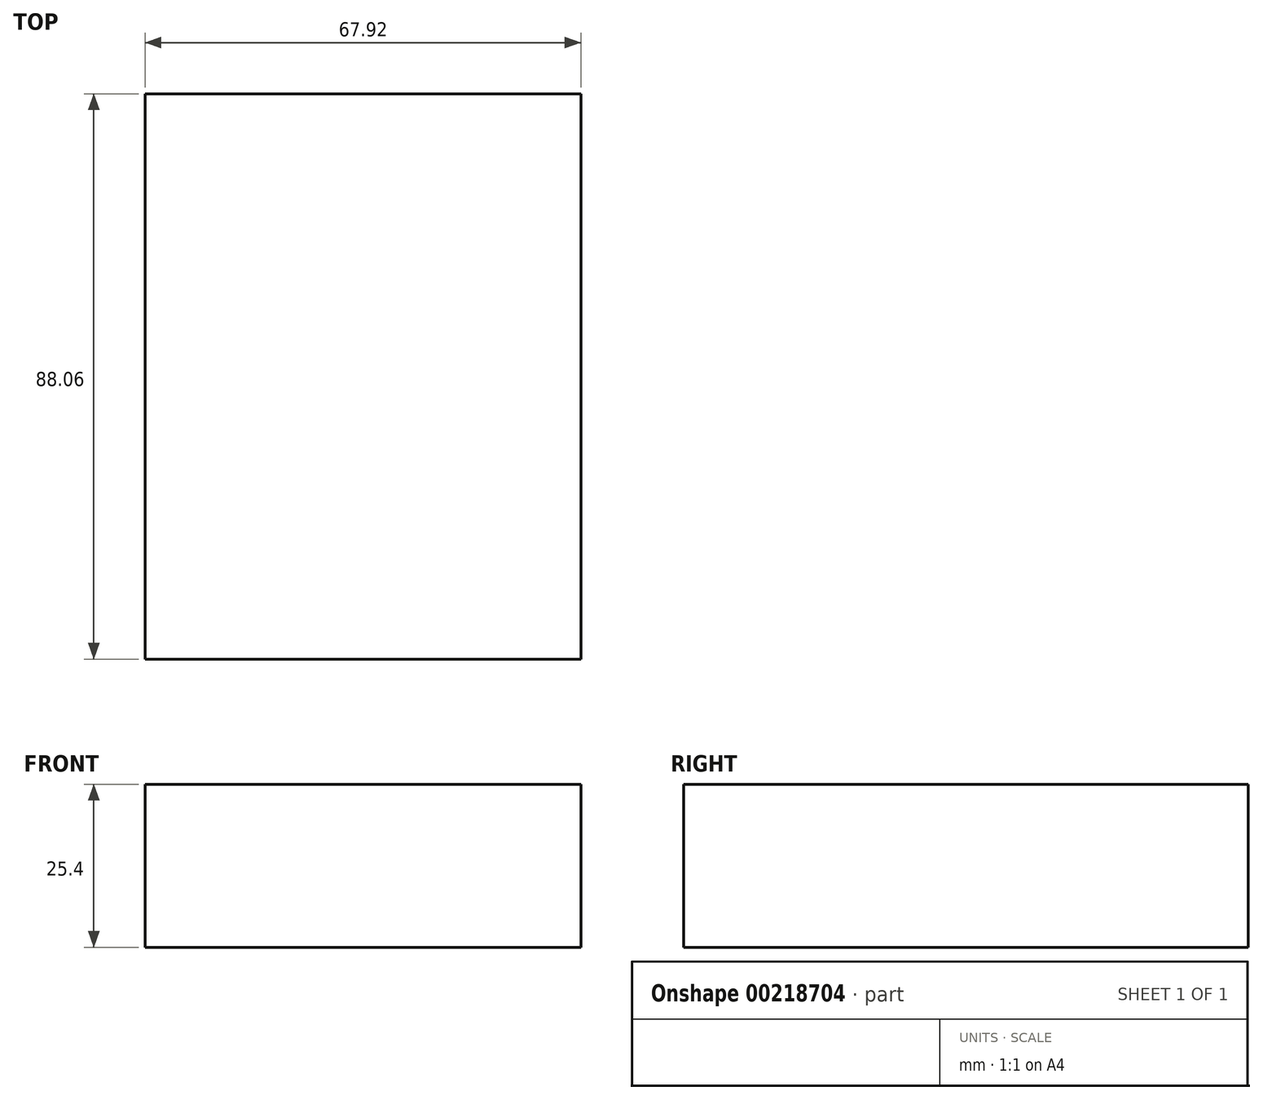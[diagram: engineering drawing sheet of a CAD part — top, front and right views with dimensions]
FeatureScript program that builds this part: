
annotation { "Feature Type Name" : "Feature", "Feature Type Description" : "" }
export const myFeature = defineFeature(function(context is Context, id is Id, definition is map)
    precondition{}
    {
        {
            var Q0;
            Q0=qCreatedBy(makeId("Top.planeOp"),FACE);
            var sketch = newSketch(context, id + "F0", { "sketchPlane" : qUnion([Q0])});
            skLineSegment(sketch, "E0.bottom", {"start": v(33.96, 44.03) * mm, "end": v(-33.96, 44.03) * mm});
            skLineSegment(sketch, "E0.top", {"start": v(33.96, -44.03) * mm, "end": v(-33.96, -44.03) * mm});
            skLineSegment(sketch, "E0.left", {"start": v(33.96, 44.03) * mm, "end": v(33.96, -44.03) * mm});
            skLineSegment(sketch, "E0.right", {"start": v(-33.96, 44.03) * mm, "end": v(-33.96, -44.03) * mm});
            skPoint(sketch, "E0.middle", {"position": v(0, 0) * mm});
            skSolve(sketch);
        }
        {
            var Q0;
            Q0 = qSketchRegion(id + "F0", true);
            extrude(context, id + "F1", {"entities" : qUnion([Q0]), "depth" : 25.4 * mm});
        }
        {
            var Q0;
            Q0=makeQuery(id+"F0.imprint","IMPRINT",FACE,{"disambiguationData":[TD([[makeQuery(id+"F0.imprint","IMPRINT",EDGE,{"derivedFrom":sQuery(id+"F0.wireOp",EDGE,"E0.bottom")}),1.0]])]});
            extrude(context, id + "F2", {"entities" : qUnion([Q0]), "depth" : 25.4 * mm});
        }
    });
